# Revit family: Legrand_Emergencia_URA21LED_EN
name_source: partatom
category: Luminaires
units: mm (PartAtom-declared; Revit-internal decimal feet)

## family parameters
Cote de connecteur circulaire = Utiliser le diamètre
Couper avec des vides une fois chargée = Non
Hôte = Face
Partagée = Non
Point de calcul de pièce = Non
Source d'éclairage = Oui
Type d'élément = Normal

## types (16) — shared parameters
Angle de l'inclinaison = 90.00°
BAES_FULL_WARRANTY_PERIOD = 2
CATEGORY = Self-contained
COLOUR_HOUSING = White
Elévation par défaut = 1219 mm
FUNCTION = EL unit
Filtre de couleur = 16777215
General Conditions of Use = https://export.legrand.com
Gradation des changements de température de couleur de lampe = <Aucun>
HEIGHT/DEPTH = 57.5
LABELLING_TYPE = Sticker
LAMP_TYPE = LED not exchangeable
LENGTH = 244
MATERIAL_COVER = Plastic. opal
MATERIAL_HOUSING = Plastic
MOUNTING_METHOD = Built-in
NOMINAL_VOLTAGE_(MAX) = 230
NOMINAL_VOLTAGE_(MIN) = 230
POWER_SUPPLY_SYSTEM = Peripheral (individual battery)
PRODUCT_FORMAT = Rectangle
PROTECTION_CLASS = II
VOLTAGE_TYPE = AC
WIDTH = 109

## per-type parameters (varying)
| type | ARTICLE_NUMBER | AUTONOMY | BATTERY_QUALITY | DEGREE_OF_PROTECTION_(IP) | Fichier de distribution photométrique | LAMP_POWER | LUMINOUS_FLUX_AT_EMERGENCY_OPERATION | MONITORING_EQUIPEMENT | REF_SPARE_BATTERY | WIRING_SYSTEM |
| URA21 LED NM 70LM 1H IP42 STD | 661601 | 1 | NiCd | IP42 | 661601.ies | 7 | 70 | None | 660972 | Standby switching |
| URA21 LED NM 100LM 1H IP42 STD | 661602 | 1 | NiCd | IP42 | 661602.ies | 10 | 100 | None | 660972 | Standby switching |
| URA21 LED M-NM 100LM 1H IP42 STD | 661603 | 1 | NiCd | IP42 | 661603.ies | 10 | 100 | None | 660972 | Continuous circuit/emergency cicuit |
| URA21 LED NM 160LM 1H IP42 STD | 661605 | 1 | NiCd | IP42 | 661605.ies | 16 | 160 | None | 660972 | Standby switching |
| URA21 LED M-NM 200LM 1H IP42 STD | 661606 | 1 | NiCd | IP42 | 661606.ies | 20 | 200 | None | 660962 | Continuous circuit/emergency cicuit |
| URA21 LED M-NM 350LM 1H IP42 STD | 661607 | 1 | NiCd | IP42 | 661607.ies | 35 | 350 | None | 660962 | Continuous circuit/emergency cicuit |
| URA21LED NM 200LM 1H IP42 STD | 661608 | 1 | NiCd | IP42 | 661608.ies | 20 | 200 | None | 660972 | Standby switching |
| URA21LED NM 350LM 1H IP42 STD | 661609 | 1 | NiCd | IP42 | 661609.ies | 35 | 350 | None | 660962 | Standby switching |
| URA21 LED M-NM 100LM 3H IP42 STD | 661610 | 3 | NiMh | IP42 | 661610.ies | 10 | 100 | None | 660971 | Continuous circuit/emergency cicuit |
| URA21LED NM 90LM 3H IP42 STD | 661611 | 3 | NiCd | IP43 | 661611.ies | 10 | 90 | None | 660962 | Continuous circuit/emergency cicuit |
| URA21 LED M-NM 200LM 2H IP42 STD | 661612 | 2 | NiMh | IP42 | 661612.ies | 20 | 200 | None | 660971 | Continuous circuit/emergency cicuit |
| URA21 LED M-NM 100LM 1H IP42 ADR | 662603 | 1 | NiCd | IP42 | 662603.ies | 10 | 100 | Automatic self test | 660972 | Continuous circuit/emergency cicuit |
| URA21 LED M-NM 200LM 1H IP42 ADR | 662606 | 1 | NiCd | IP42 | 662606.ies | 20 | 200 | Automatic self test | 660962 | Continuous circuit/emergency cicuit |
| URA21 LED M-NM 350LM 1H IP42 ADR | 662607 | 1 | NiMh | IP42 | 662607.ies | 35 | 350 | Automatic self test | 660971 | Continuous circuit/emergency cicuit |
| URA21 LED M-NM 100LM 3H IP42 ADR | 662610 | 3 | NiMh | IP42 | 662610.ies | 10 | 100 | Automatic self test | 660971 | Continuous circuit/emergency cicuit |
| URA21 LED M-NM 200LM 2H IP42 ADR | 662612 | 2 | NiMh | IP42 | 662612.ies | 20 | 200 | Automatic self test | 660971 | Continuous circuit/emergency cicuit |

note: column(s) folded — value = type name in every type: DESCRIPTION
